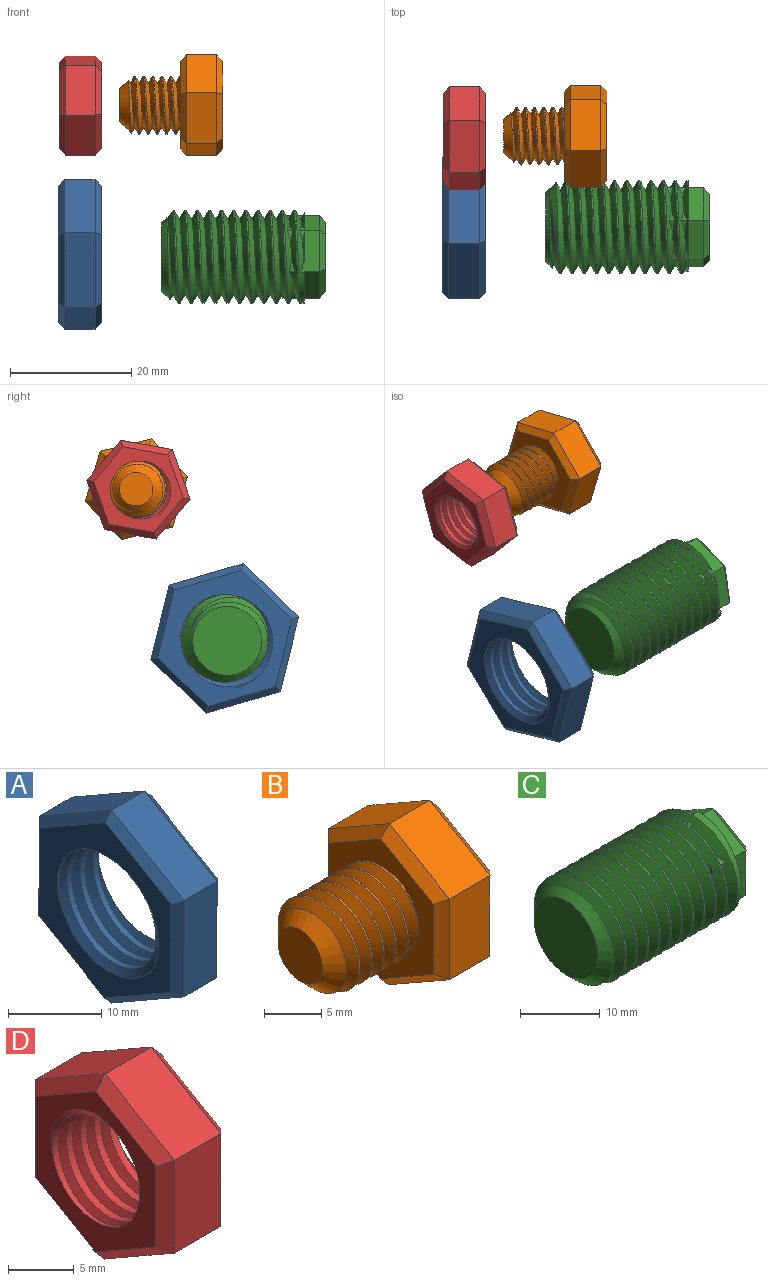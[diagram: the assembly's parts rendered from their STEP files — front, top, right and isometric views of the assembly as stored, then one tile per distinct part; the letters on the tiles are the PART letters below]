
ASSEMBLY  parts=4 mates=2
PART A: 23 faces, bbox 9.3x22.7x26 mm
  f0: cylinder r=7.24mm len=14.48mm, axis (1,0,0), area 111.6mm2, adj f7,f8,f21,f22
  f1: plane 10.98x6.38mm, normal (0,-0.5,0.86), area 63.5mm2, adj f2,f6,f14,f18
  f2: plane 12.7x5mm, normal (0,-1,0), area 63.5mm2, adj f1,f3,f12,f16
  f3: plane 11.02x6.32mm, normal (0,-0.5,-0.87), area 63.5mm2, adj f2,f4,f10,f15
  f4: plane 10.98x6.38mm, normal (0,0.5,-0.86), area 63.5mm2, adj f3,f5,f9,f17
  f5: plane 12.7x5mm, normal (0,1,0), area 63.5mm2, adj f4,f6,f11,f19
  f6: plane 11.02x6.32mm, normal (0,0.5,0.87), area 63.5mm2, adj f1,f5,f13,f20
  f7: plane 23.73x20.67mm, normal (-1,0,0), area 164.4mm2, adj f0,f9,f10,f11,f12,f13,f14,f21
  f8: plane 23.73x20.67mm, normal (1,0,0), area 164.4mm2, adj f0,f15,f16,f17,f18,f19,f20,f21
  f9: plane 10.99x6.96mm, normal (-0.71,0.36,-0.61), area 17.1mm2, adj f4,f7,f10,f11
  f10: plane 11.02x6.9mm, normal (-0.71,-0.35,-0.61), area 17.1mm2, adj f3,f7,f9,f12
  f11: plane 12.7x1.03mm, normal (-0.71,0.71,0), area 17.1mm2, adj f5,f7,f9,f13
  f12: plane 12.7x1.03mm, normal (-0.71,-0.71,0), area 17.1mm2, adj f2,f7,f10,f14
  f13: plane 11.02x6.9mm, normal (-0.71,0.35,0.61), area 17.1mm2, adj f6,f7,f11,f14
  f14: plane 10.99x6.96mm, normal (-0.71,-0.36,0.61), area 17.1mm2, adj f1,f7,f12,f13
  f15: plane 11.02x6.9mm, normal (0.71,-0.35,-0.61), area 17.1mm2, adj f3,f8,f16,f17
  f16: plane 12.7x1.03mm, normal (0.71,-0.71,0), area 17.1mm2, adj f2,f8,f15,f18
  f17: plane 10.99x6.96mm, normal (0.71,0.36,-0.61), area 17.1mm2, adj f4,f8,f15,f19
  f18: plane 10.99x6.96mm, normal (0.71,-0.36,0.61), area 17.1mm2, adj f1,f8,f16,f20
  f19: plane 12.7x1.03mm, normal (0.71,0.71,0), area 17.1mm2, adj f5,f8,f17,f20
  f20: plane 11.02x6.9mm, normal (0.71,0.35,0.61), area 17.1mm2, adj f6,f8,f18,f19
  f21: bspline ~19.31x16.73mm, area 223mm2, adj f0,f7,f8,f22
  f22: bspline ~19.31x16.73mm, area 223mm2, adj f0,f7,f8,f21
PART B: 25 faces, bbox 17.8x15.9x18.1 mm
  f0: cylinder r=4.75mm len=9.5mm, axis (1,0,0), area 28.1mm2, adj f1,f2,f4,f12
  f1: bspline ~10.97x9.91mm, area 196.7mm2, adj f0,f2,f4,f12
  f2: bspline ~10.97x10.66mm, area 196.6mm2, adj f0,f1,f4,f12
  f3: plane 5.5x5.5mm, normal (-1,0,0), area 23.8mm2, adj f4
  f4: cone r=4.75mm half-angle=45deg, axis (1,0,0), area 47.4mm2, adj f0,f1,f2,f3
  f5: plane 7.48x5mm, normal (0,-0.5,0.86), area 43.3mm2, adj f6,f10,f18,f22
  f6: plane 8.66x5mm, normal (0,-1,0), area 43.3mm2, adj f5,f7,f16,f20
  f7: plane 7.52x5mm, normal (0,-0.5,-0.87), area 43.3mm2, adj f6,f8,f14,f19
  f8: plane 7.48x5mm, normal (0,0.5,-0.86), area 43.3mm2, adj f7,f9,f13,f21
  f9: plane 8.66x5mm, normal (0,1,0), area 43.3mm2, adj f8,f10,f15,f23
  f10: plane 7.52x5mm, normal (0,0.5,0.87), area 43.3mm2, adj f5,f9,f17,f24
  f11: plane 15.01x13.03mm, normal (1,0,0), area 146.4mm2, adj f13,f14,f15,f16,f17,f18
  f12: plane 15.83x13.85mm, normal (-1,0,0), area 89.2mm2, adj f0,f1,f2,f19,f20,f21,f22,f23
  f13: plane 7.49x4.93mm, normal (0.71,0.36,-0.61), area 11.4mm2, adj f8,f11,f14,f15
  f14: plane 7.52x4.88mm, normal (0.71,-0.35,-0.61), area 11.4mm2, adj f7,f11,f13,f16
  f15: plane 8.66x1.03mm, normal (0.71,0.71,0), area 11.4mm2, adj f9,f11,f13,f17
  f16: plane 8.66x1.03mm, normal (0.71,-0.71,0), area 11.4mm2, adj f6,f11,f14,f18
  f17: plane 7.52x4.88mm, normal (0.71,0.35,0.61), area 11.4mm2, adj f10,f11,f15,f18
  f18: plane 7.49x4.93mm, normal (0.71,-0.36,0.61), area 11.4mm2, adj f5,f11,f16,f17
  f19: plane 7.52x4.88mm, normal (-0.71,-0.35,-0.61), area 11.4mm2, adj f7,f12,f20,f21
  f20: plane 8.66x1.03mm, normal (-0.71,-0.71,0), area 11.4mm2, adj f6,f12,f19,f22
  f21: plane 7.49x4.93mm, normal (-0.71,0.36,-0.61), area 11.4mm2, adj f8,f12,f19,f23
  f22: plane 7.49x4.93mm, normal (-0.71,-0.36,0.61), area 11.4mm2, adj f5,f12,f20,f24
  f23: plane 8.66x1.03mm, normal (-0.71,0.71,0), area 11.4mm2, adj f9,f12,f21,f24
  f24: plane 7.52x4.88mm, normal (-0.71,0.35,0.61), area 11.4mm2, adj f10,f12,f22,f23
PART C: 45 faces, bbox 27.9x17.9x15.5 mm
  f0: plane 4.29x2.47mm, normal (1,0,0), area 1.5mm2, adj f8,f18
  f1: bspline ~23.88x17.74mm, area 827.6mm2, adj f2,f4,f5,f6,f9,f11,f12,f13
  f2: cylinder r=7.68mm len=21.5mm, axis (1,0,0), area 114.8mm2, adj f1,f4,f6,f7,f9
  f3: plane 11.36x11.36mm, normal (-1,0,0), area 101.4mm2, adj f5
  f4: plane 15.36x14.74mm, normal (1,0,0), area 44.6mm2, adj f1,f2,f7,f18,f19,f20,f21,f22
  f5: cone r=7.68mm half-angle=45deg, axis (1,0,0), area 63.2mm2, adj f1,f3,f6,f9
  f6: cone r=7.68mm half-angle=45deg, axis (1,0,0), area 13.2mm2, adj f1,f2,f5,f9
  f7: plane 0.88x0.78mm, normal (0,1,0), area 0.5mm2, adj f2,f4,f9,f18
  f8: bspline ~6.65x4.6mm, area 1.4mm2, adj f0,f9,f18
  f9: bspline ~24.21x17.74mm, area 816mm2, adj f1,f2,f5,f6,f7,f8,f10,f11
  f10: plane 1.82x0.82mm, normal (-1,0,0), area 0.4mm2, adj f9,f11,f12
  f11: plane 1.97x1.2mm, normal (0,-0.49,-0.87), area 0.7mm2, adj f1,f9,f10,f12
  f12: plane 2.23x0.79mm, normal (0,-1,-0.01), area 0.6mm2, adj f1,f9,f10,f11
  f13: plane 1.97x1.2mm, normal (0,0.49,0.87), area 0.8mm2, adj f1,f9,f14
  f14: plane 1.95x1.22mm, normal (0,-0.51,0.86), area 0.8mm2, adj f1,f9,f13
  f15: plane 1.97x1.2mm, normal (0,0.49,0.87), area 0.8mm2, adj f1,f9,f16
  f16: plane 2.24x1.07mm, normal (0,1,0.01), area 0.8mm2, adj f1,f9,f15
  f17: plane 11.55x10.03mm, normal (1,0,0), area 86.6mm2, adj f39,f40,f41,f42,f43,f44
  f18: plane 6.2x3.61mm, normal (0,0.49,0.87), area 18.5mm2, adj f0,f4,f7,f8,f9,f19,f23,f43
  f19: plane 7.11x3.46mm, normal (0,1,0.01), area 18.1mm2, adj f1,f4,f9,f18,f20,f41
  f20: plane 5.98x3.5mm, normal (0,0.51,-0.86), area 17.3mm2, adj f4,f19,f21,f39
  f21: plane 6.02x3.43mm, normal (0,-0.49,-0.87), area 17.3mm2, adj f4,f20,f22,f40
  f22: plane 6.93x2.5mm, normal (0,-1,-0.01), area 17.3mm2, adj f4,f21,f23,f42
  f23: plane 5.98x3.5mm, normal (0,-0.51,0.86), area 17.3mm2, adj f4,f18,f22,f44
  f24: plane 2.24x1.07mm, normal (0,1,0.01), area 0.8mm2, adj f1,f9,f25
  f25: plane 1.95x1.22mm, normal (0,0.51,-0.86), area 0.8mm2, adj f1,f9,f24
  f26: plane 2.24x1.07mm, normal (0,1,0.01), area 0.8mm2, adj f1,f9,f27
  f27: plane 1.95x1.22mm, normal (0,0.51,-0.86), area 0.8mm2, adj f1,f9,f26
  f28: plane 1.95x1.22mm, normal (0,0.51,-0.86), area 0.8mm2, adj f1,f9,f29
  f29: plane 1.97x1.2mm, normal (0,-0.49,-0.87), area 0.8mm2, adj f1,f9,f28
  f30: plane 1.95x1.22mm, normal (0,0.51,-0.86), area 0.8mm2, adj f1,f9,f31
  f31: plane 1.97x1.2mm, normal (0,-0.49,-0.87), area 0.8mm2, adj f1,f9,f30
  f32: plane 1.97x1.2mm, normal (0,-0.49,-0.87), area 0.8mm2, adj f1,f9,f33
  f33: plane 2.24x1.07mm, normal (0,-1,-0.01), area 0.8mm2, adj f1,f9,f32
  f34: plane 2.24x1.07mm, normal (0,-1,-0.01), area 0.8mm2, adj f1,f9,f35
  f35: plane 1.95x1.22mm, normal (0,-0.51,0.86), area 0.8mm2, adj f1,f9,f34
  f36: plane 0.84x0.5mm, normal (0,-0.51,0.86), area 0.1mm2, adj f1,f37,f38
  f37: plane 1.47x0.36mm, normal (0,-1,-0.01), area 0.2mm2, adj f1,f36,f38
  f38: plane 1.87x0.82mm, normal (-1,0,0), area 0.4mm2, adj f1,f36,f37
  f39: plane 5.99x4.07mm, normal (0.71,0.36,-0.61), area 9mm2, adj f17,f20,f40,f41
  f40: plane 6.02x4.01mm, normal (0.71,-0.35,-0.61), area 9mm2, adj f17,f21,f39,f42
  f41: plane 6.93x1.04mm, normal (0.71,0.71,0), area 9mm2, adj f17,f19,f39,f43
  f42: plane 6.93x1.04mm, normal (0.71,-0.71,0), area 9mm2, adj f17,f22,f40,f44
  f43: plane 6.02x4.01mm, normal (0.71,0.35,0.61), area 9mm2, adj f17,f18,f41,f44
  f44: plane 5.99x4.07mm, normal (0.71,-0.36,0.61), area 9mm2, adj f17,f23,f42,f43
PART D: 23 faces, bbox 9.1x15.4x17.7 mm
  f0: plane 7.49x5mm, normal (0,-0.5,0.86), area 43.3mm2, adj f1,f5,f13,f17
  f1: plane 8.66x5mm, normal (0,-1,0), area 43.3mm2, adj f0,f2,f11,f15
  f2: plane 7.51x5mm, normal (0,-0.5,-0.87), area 43.3mm2, adj f1,f3,f9,f14
  f3: plane 7.49x5mm, normal (0,0.5,-0.86), area 43.3mm2, adj f2,f4,f8,f16
  f4: plane 8.66x5mm, normal (0,1,0), area 43.3mm2, adj f3,f5,f10,f18
  f5: plane 7.51x5mm, normal (0,0.5,0.87), area 43.3mm2, adj f0,f4,f12,f19
  f6: plane 15.37x13.38mm, normal (-1,0,0), area 71.4mm2, adj f8,f9,f10,f11,f12,f13,f20,f21
  f7: plane 15.37x13.38mm, normal (1,0,0), area 71.4mm2, adj f14,f15,f16,f17,f18,f19,f20,f21
  f8: plane 7.49x4.93mm, normal (-0.71,0.36,-0.61), area 11.4mm2, adj f3,f6,f9,f10
  f9: plane 7.51x4.89mm, normal (-0.71,-0.35,-0.61), area 11.4mm2, adj f2,f6,f8,f11
  f10: plane 8.66x1.02mm, normal (-0.71,0.71,0), area 11.4mm2, adj f4,f6,f8,f12
  f11: plane 8.66x1.02mm, normal (-0.71,-0.71,0), area 11.4mm2, adj f1,f6,f9,f13
  f12: plane 7.51x4.89mm, normal (-0.71,0.35,0.61), area 11.4mm2, adj f5,f6,f10,f13
  f13: plane 7.49x4.93mm, normal (-0.71,-0.36,0.61), area 11.4mm2, adj f0,f6,f11,f12
  f14: plane 7.51x4.89mm, normal (0.71,-0.35,-0.61), area 11.4mm2, adj f2,f7,f15,f16
  f15: plane 8.66x1.02mm, normal (0.71,-0.71,0), area 11.4mm2, adj f1,f7,f14,f17
  f16: plane 7.49x4.93mm, normal (0.71,0.36,-0.61), area 11.4mm2, adj f3,f7,f14,f18
  f17: plane 7.49x4.93mm, normal (0.71,-0.36,0.61), area 11.4mm2, adj f0,f7,f15,f19
  f18: plane 8.66x1.02mm, normal (0.71,0.71,0), area 11.4mm2, adj f4,f7,f16,f19
  f19: plane 7.51x4.89mm, normal (0.71,0.35,0.61), area 11.4mm2, adj f5,f7,f17,f18
  f20: cylinder r=4.66mm len=9.32mm, axis (1,0,0), area 85.4mm2, adj f6,f7,f21,f22
  f21: bspline ~12.5x10.82mm, area 128.4mm2, adj f6,f7,f20,f22
  f22: bspline ~12.5x10.82mm, area 128.5mm2, adj f6,f7,f20,f21
PLACE A rot(axis=(0,0.6,-0.8),180deg) t=(-55.27,-6.86,23.48)mm fixed
PLACE B rot(axis=(-1,0,0),43.8deg) t=(-31.66,7.73,48.08)mm
PLACE C rot(axis=(1,0,0),109.9deg) t=(-14.77,-7.25,23.06)mm
PLACE D rot(axis=(1,0,0),100.2deg) t=(-48.16,7.38,48.02)mm fixed
MATE cylindrical C.f2 <-> A.f7  axis (-1,0,0) through (-38.27,-7.25,23.06)mm
MATE cylindrical B.f0 <-> D.f6  axis (-1,0,0) through (-45.16,7.73,48.08)mm
